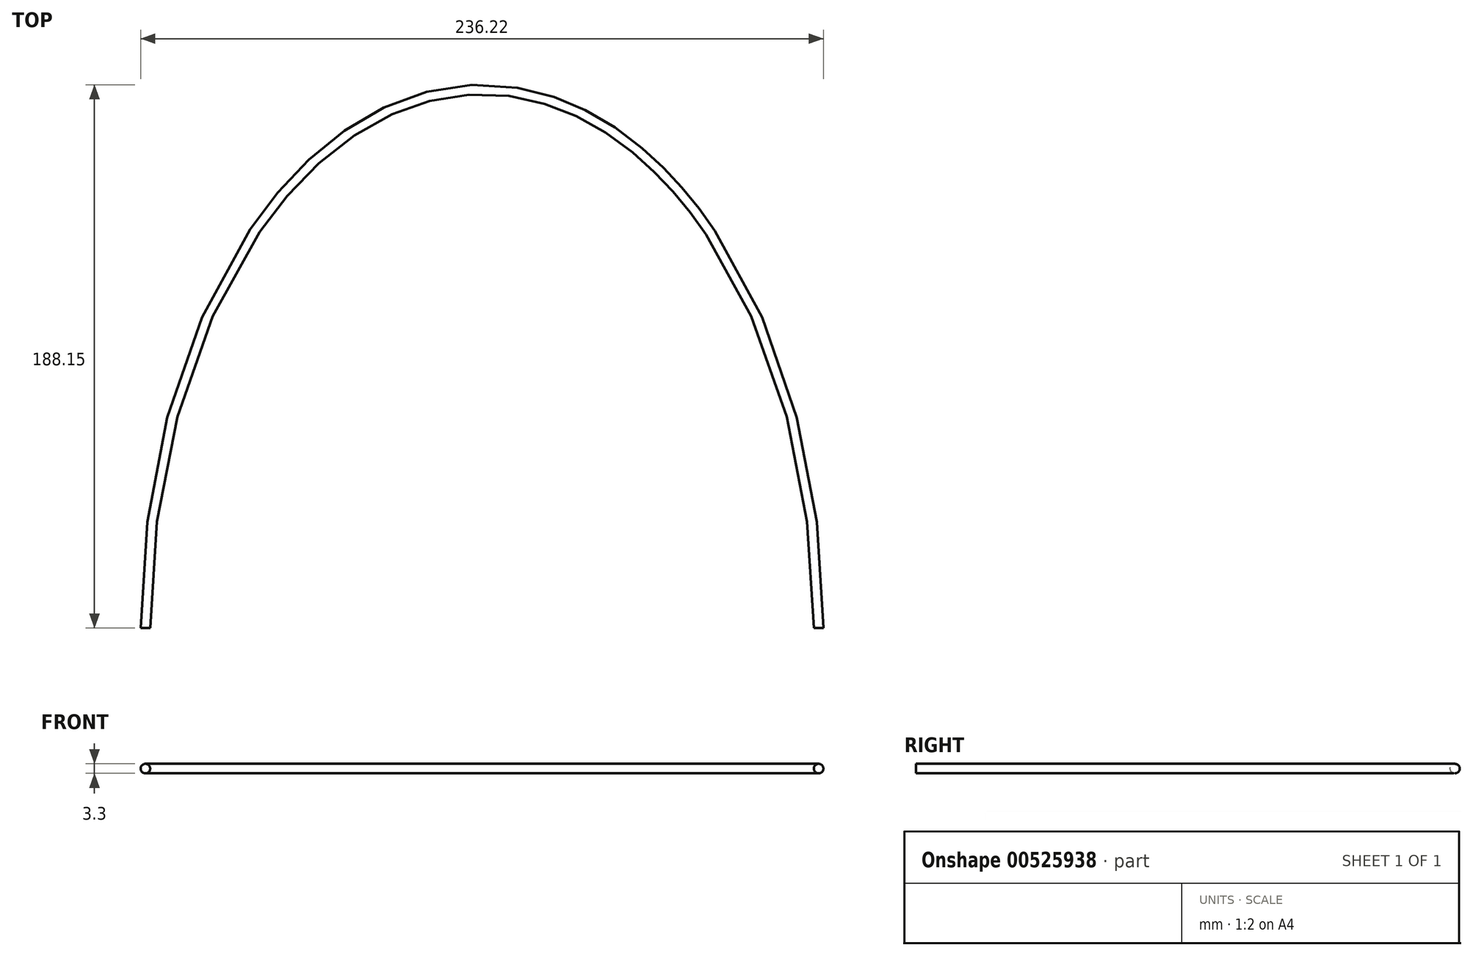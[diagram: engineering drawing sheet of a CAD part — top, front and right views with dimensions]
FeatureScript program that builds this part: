
annotation { "Feature Type Name" : "Feature", "Feature Type Description" : "" }
export const myFeature = defineFeature(function(context is Context, id is Id, definition is map)
    precondition{}
    {
        {
            var Q0;
            Q0=qCreatedBy(makeId("Top.planeOp"),FACE);
            var sketch = newSketch(context, id + "F0", { "sketchPlane" : qUnion([Q0])});
            skLineSegment(sketch, "E0", {"start": v(0, 0) * mm, "end": v(116.46, 0) * mm, "construction": true});
            skLineSegment(sketch, "E1", {"start": v(0, 0) * mm, "end": v(-116.46, 0) * mm, "construction": true});
            skEllipticalArc(sketch, "E2", {});
            const initialGuessF0  = {"E2": [0, 0, 1, 0, 0.116459, 0.18651013687507859, 6.283185307179586, 3.141592653589793]};
            skSetInitialGuess(sketch, initialGuessF0);
            skSolve(sketch);
        }
        {
            var Q0;
            Q0=qCreatedBy(makeId("Front.planeOp"),FACE);
            var sketch = newSketch(context, id + "F1", { "sketchPlane" : qUnion([Q0])});
            skLineSegment(sketch, "E3", {"start": v(0, 0) * mm, "end": v(116.46, 0) * mm, "construction": true});
            skCircle(sketch, "E4", {"center": v(116.46, 0) * mm, "radius": 1.65 * mm});
            skSolve(sketch);
        }
        {
            var Q0;
            Q0=makeQuery(id+"F1.imprint","IMPRINT",FACE,{"disambiguationData":[TD([[makeQuery(id+"F1.imprint","IMPRINT",EDGE,{"derivedFrom":sQuery(id+"F1.wireOp",EDGE,"E4")}),1.0]])]});
            var Q1;
            Q1=sQuery(id+"F0.wireOp",EDGE,"E2");
            sweep(context, id + "F2", {"profiles" : qUnion([Q0]), "path" : qUnion([Q1])});
        }
    });
